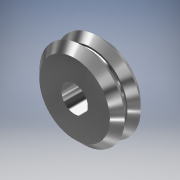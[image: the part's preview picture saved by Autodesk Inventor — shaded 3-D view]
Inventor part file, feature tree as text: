
AUTODESK INVENTOR PART (.ipt)
format: ipt  version: 2017 SP1 (Build 210196100, 196)  size: 140,800 bytes
history: native  units: in
note: dims shown in document units (in); Inventor stores cm internally (conversion verified against a paired STEP export)
features: revolve x1, sketch x1
ambient origin geometry x8: Origin, YZ Plane, XZ Plane, XY Plane, X Axis, Y Axis, Z Axis, Center Point
bodies: Solid1 (feature_tree)
feature tree (2):
  revolve  "Revolution1"  [1 undecoded]
  sketch  "Sketch1"  dims[d0=0.1875in d1=0.5in d3=0.04in d4=0.436in d5=90.0deg d6=0.605in d7=0.226in]
note: 1 required parameter value undecoded (feature->parameter linkage not recoverable at this tier; creation-order binding heuristic only, values carry confidence <= 0.55)
